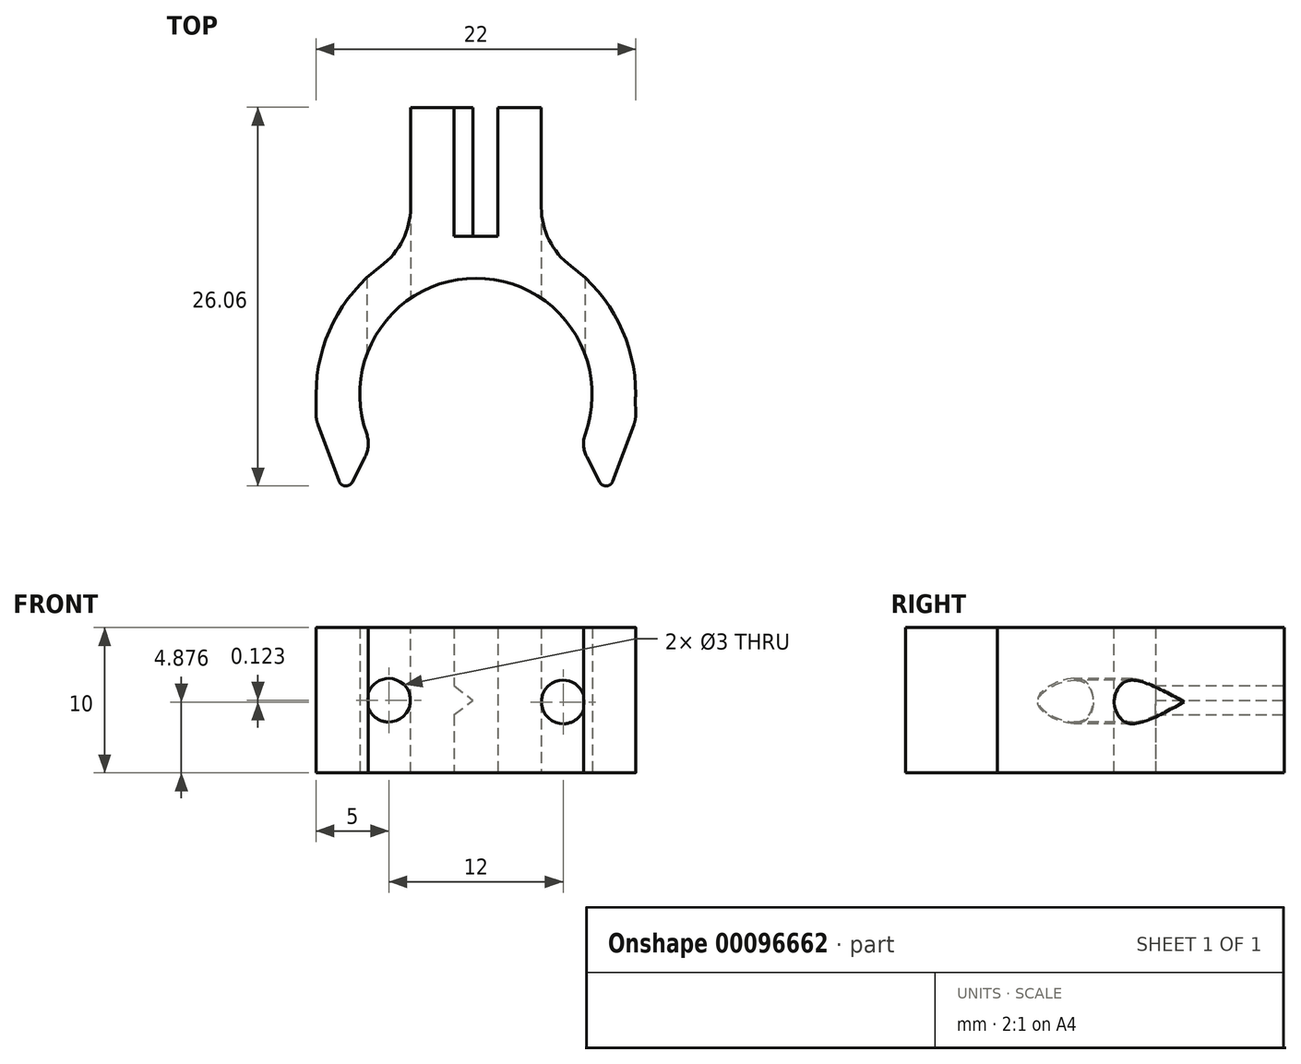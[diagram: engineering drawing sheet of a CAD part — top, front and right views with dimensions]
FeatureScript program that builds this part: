
annotation { "Feature Type Name" : "Feature", "Feature Type Description" : "" }
export const myFeature = defineFeature(function(context is Context, id is Id, definition is map)
    precondition{}
    {
        {
            var Q0;
            Q0=qCreatedBy(makeId("Top.planeOp"),FACE);
            var sketch = newSketch(context, id + "F0", { "sketchPlane" : qUnion([Q0])});
            skArc(sketch, "E0", {"start": v(7.83, -1.65) * mm, "mid": v(0, 8) * mm, "end": v(-7.83, -1.65) * mm});
            skArc(sketch, "E1.0", {"start": v(11, 0) * mm, "mid": v(9.23, 5.98) * mm, "end": v(4.5, 10.04) * mm});
            skPoint(sketch, "E2.endSnap0", {"position": v(0, 11) * mm});
            skLineSegment(sketch, "E3", {"start": v(1.5, 11.3) * mm, "end": v(1.5, 16.76) * mm});
            skLineSegment(sketch, "E4", {"start": v(-1.5, 16.76) * mm, "end": v(-1.5, 11.3) * mm});
            skLineSegment(sketch, "E5", {"start": v(-1.5, 11.3) * mm, "end": v(-1.5, 10.9) * mm});
            skLineSegment(sketch, "E6", {"start": v(1.5, 10.9) * mm, "end": v(1.5, 11.3) * mm});
            skArc(sketch, "E7.trimOffspring", {"start": v(-4.68, 9.96) * mm, "mid": v(-9.29, 5.9) * mm, "end": v(-11, 0) * mm});
            skPoint(sketch, "E2.end.orphan", {"position": v(0, 16.76) * mm});
            skPoint(sketch, "E8.orphan", {"position": v(1.5, 9.71) * mm});
            skLineSegment(sketch, "E9.0", {"start": v(-4.5, 19.76) * mm, "end": v(-4.5, 11.3) * mm});
            skLineSegment(sketch, "E9.1", {"start": v(-4.5, 19.76) * mm, "end": v(-1.5, 19.76) * mm});
            skLineSegment(sketch, "E9.2", {"start": v(4.5, 11.3) * mm, "end": v(4.5, 19.76) * mm});
            skLineSegment(sketch, "E10", {"start": v(-4.5, 11.3) * mm, "end": v(-4.5, 10.23) * mm});
            skLineSegment(sketch, "E11", {"start": v(4.5, 11.3) * mm, "end": v(4.5, 10.04) * mm});
            skLineSegment(sketch, "E12", {"start": v(-1.5, 16.76) * mm, "end": v(-1.5, 19.76) * mm});
            skLineSegment(sketch, "E13", {"start": v(1.5, 16.76) * mm, "end": v(1.5, 19.76) * mm});
            skLineSegment(sketch, "E14.trimOffspring", {"start": v(1.5, 19.76) * mm, "end": v(4.5, 19.76) * mm});
            skLineSegment(sketch, "E15", {"start": v(-1.5, 10.9) * mm, "end": v(1.5, 10.9) * mm});
            skPoint(sketch, "E16.orphan", {"position": v(4.5, 8.95) * mm});
            skPoint(sketch, "E17.orphan", {"position": v(-4.5, 8.95) * mm});
            skLineSegment(sketch, "E18", {"start": v(-4.5, 10.23) * mm, "end": v(-4.5, 10.05) * mm});
            skLineSegment(sketch, "E19", {"start": v(-4.5, 10.05) * mm, "end": v(-4.68, 9.96) * mm});
            skArc(sketch, "E20", {"start": v(7.53, -2.71) * mm, "mid": v(0, 8) * mm, "end": v(-7.53, -2.71) * mm});
            skLineSegment(sketch, "E21", {"start": v(11, 0) * mm, "end": v(10.98, -0.02) * mm});
            skPoint(sketch, "E22.endSnap0", {"position": v(9.1, -1.74) * mm});
            skLineSegment(sketch, "E23", {"start": v(11, -1.74) * mm, "end": v(10.97, 0.58) * mm});
            skLineSegment(sketch, "E24", {"start": v(-11, -1.74) * mm, "end": v(-11, 0) * mm});
            skLineSegment(sketch, "E25", {"start": v(-7.63, -4.3) * mm, "end": v(-8.5, -6.03) * mm});
            skLineSegment(sketch, "E26", {"start": v(-9.42, -5.97) * mm, "end": v(-11, -1.74) * mm});
            skLineSegment(sketch, "E27.MirrorCS", {"start": v(7.63, -4.3) * mm, "end": v(8.5, -6.03) * mm});
            skLineSegment(sketch, "E28.MirrorCS", {"start": v(9.42, -5.97) * mm, "end": v(11, -1.74) * mm});
            skPoint(sketch, "E29.visualSharp", {"position": v(-7.2, -3.48) * mm});
            skArc(sketch, "E29.filletArc", {"start": v(-7.63, -4.3) * mm, "mid": v(-7.41, -3.52) * mm, "end": v(-7.53, -2.71) * mm});
            skPoint(sketch, "E30.visualSharp", {"position": v(7.2, -3.48) * mm});
            skArc(sketch, "E30.filletArc", {"start": v(7.53, -2.71) * mm, "mid": v(7.41, -3.52) * mm, "end": v(7.63, -4.3) * mm});
            skPoint(sketch, "E31.visualSharp", {"position": v(-9.03, -7.04) * mm});
            skArc(sketch, "E31.filletArc", {"start": v(-9.42, -5.97) * mm, "mid": v(-8.98, -6.3) * mm, "end": v(-8.5, -6.03) * mm});
            skPoint(sketch, "E32.visualSharp", {"position": v(9.03, -7.04) * mm});
            skArc(sketch, "E32.filletArc", {"start": v(8.5, -6.03) * mm, "mid": v(8.98, -6.3) * mm, "end": v(9.42, -5.97) * mm});
            skSolve(sketch);
        }
        {
            var Q0;
            Q0 = qSketchRegion(id + "F0", true);
            extrude(context, id + "F1", {"entities" : qUnion([Q0]), "depth" : 10 * mm});
        }
        {
            var Q0;
            Q0=makeQuery(id+"F1.opExtrude","SWEPT_EDGE",EDGE,{"disambiguationData":[OSD([sQuery(id+"F0.wireOp",EDGE,"E1.0"),sQuery(id+"F0.wireOp",EDGE,"E11")])]});
            fillet(context, id + "F2", {"entities" : qUnion([Q0]), "radius" : 5 * mm, "tangentPropagation" : true, "allowEdgeOverflow" : false});
        }
        {
            var Q0;
            Q0=makeQuery(id+"F1.opExtrude","SWEPT_EDGE",EDGE,{"disambiguationData":[OSD([sQuery(id+"F0.wireOp",EDGE,"E18"),sQuery(id+"F0.wireOp",EDGE,"E19")])]});
            fillet(context, id + "F3", {"entities" : qUnion([Q0]), "radius" : 5 * mm, "tangentPropagation" : true, "allowEdgeOverflow" : false});
        }
        {
            var Q0;
            Q0=makeQuery(id+"F1.opExtrude","SWEPT_FACE",FACE,{"disambiguationData":[OSD([sQuery(id+"F0.wireOp",EDGE,"E9.1")])]});
            var sketch = newSketch(context, id + "F4", { "sketchPlane" : qUnion([Q0])});
            skLineSegment(sketch, "E33", {"start": v(0.2, 5) * mm, "end": v(1.5, 4) * mm});
            skLineSegment(sketch, "E34", {"start": v(0.2, 5) * mm, "end": v(1.5, 6) * mm});
            skPoint(sketch, "E35.start.orphan", {"position": v(1.5, 5) * mm});
            skLineSegment(sketch, "E36", {"start": v(1.5, 4) * mm, "end": v(1.5, 6) * mm});
            skSolve(sketch);
        }
        {
            var Q0;
            Q0 = qSketchRegion(id + "F4", true);
            extrude(context, id + "F5", {"entities" : qUnion([Q0]), "operationType" : NewBodyOperationType.ADD, "endBound" : BoundingType.UP_TO_NEXT, "oppositeDirection" : true, "depth" : 25 * mm});
        }
        {
            var Q0;
            Q0=qCreatedBy(makeId("Front.planeOp"),FACE);
            var sketch = newSketch(context, id + "F6", { "sketchPlane" : qUnion([Q0])});
            skCircle(sketch, "E37", {"center": v(-6, 5) * mm, "radius": 1.5 * mm});
            skCircle(sketch, "E38", {"center": v(6, 4.88) * mm, "radius": 1.5 * mm});
            skSolve(sketch);
        }
        {
            var Q0;
            Q0 = qSketchRegion(id + "F6", true);
            extrude(context, id + "F7", {"entities" : qUnion([Q0]), "operationType" : NewBodyOperationType.REMOVE, "oppositeDirection" : true, "depth" : 25 * mm});
        }
        {
            var Q0;
            Q0=makeQuery(id+"F1.opExtrude","SWEPT_EDGE",EDGE,{"disambiguationData":[OSD([sQuery(id+"F0.wireOp",EDGE,"E22"),sQuery(id+"F0.wireOp",EDGE,"E23")])]});
            var Q1;
            Q1=makeQuery(id+"F1.opExtrude","SWEPT_EDGE",EDGE,{"disambiguationData":[OSD([sQuery(id+"F0.wireOp",EDGE,"8C0J0EUD-2DJ0-HEAS-Sm04-guAnvUFQOOck"),sQuery(id+"F0.wireOp",EDGE,"E24")])]});
            fillet(context, id + "F8", {"entities" : qUnion([Q0, Q1]), "radius" : 2 * mm, "tangentPropagation" : true, "allowEdgeOverflow" : false});
        }
    });
